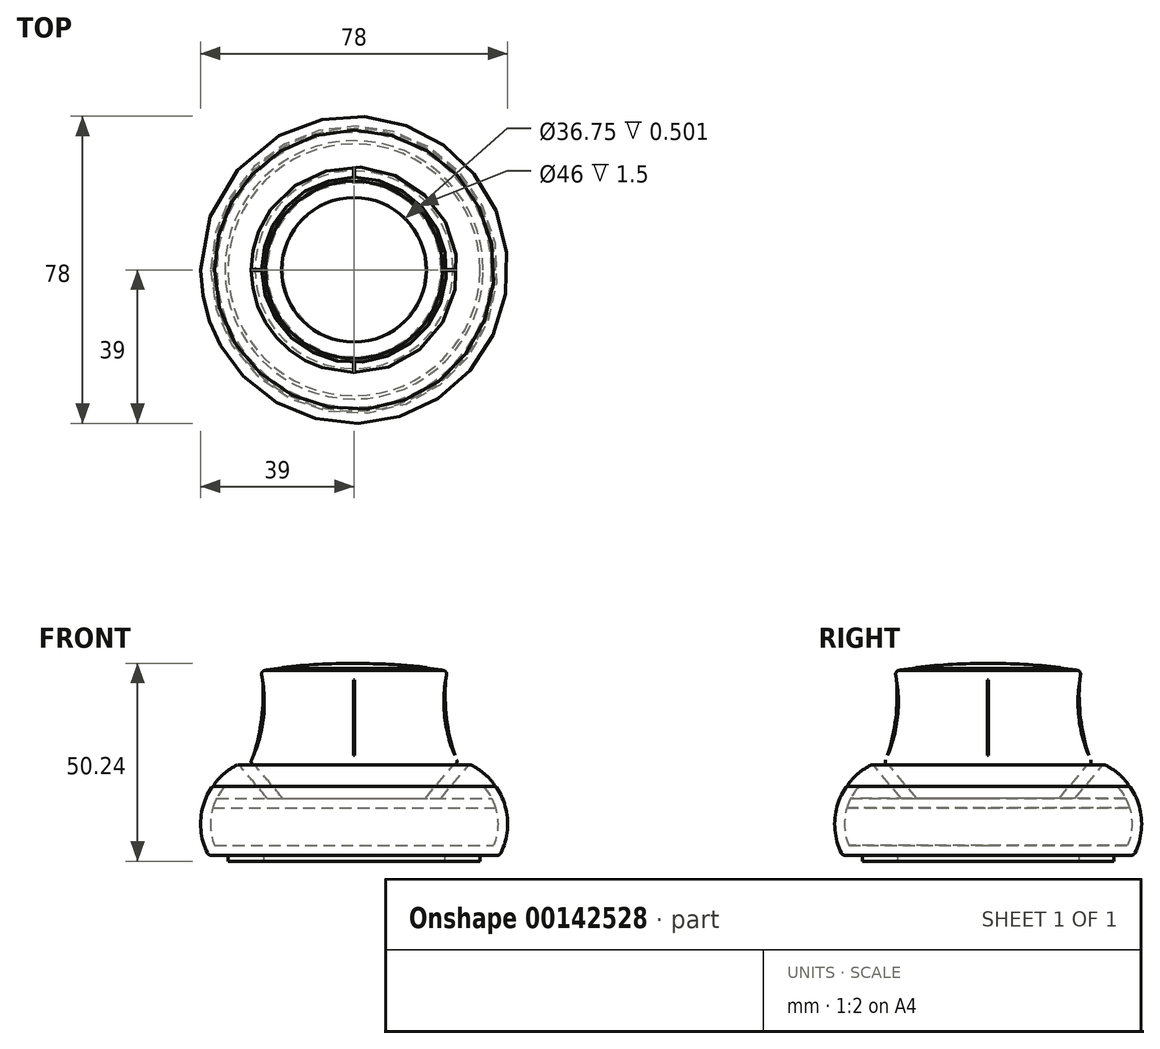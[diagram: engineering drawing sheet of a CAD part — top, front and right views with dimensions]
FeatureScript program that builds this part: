
annotation { "Feature Type Name" : "Feature", "Feature Type Description" : "" }
export const myFeature = defineFeature(function(context is Context, id is Id, definition is map)
    precondition{}
    {
        {
            var Q0;
            Q0=qCreatedBy(makeId("Front.planeOp"),FACE);
            var sketch = newSketch(context, id + "F0", { "sketchPlane" : qUnion([Q0])});
            skLineSegment(sketch, "E0", {"start": v(36.39, 0) * mm, "end": v(0, 0) * mm});
            skLineSegment(sketch, "E1", {"start": v(0, 0) * mm, "end": v(0, 17.5) * mm, "construction": true});
            skLineSegment(sketch, "E2", {"start": v(32.81, 17.5) * mm, "end": v(35.74, 17.5) * mm});
            skArc(sketch, "E3", {"start": v(35.4, 18.3) * mm, "mid": v(32.8, 20.95) * mm, "end": v(29.67, 22.95) * mm});
            skArc(sketch, "E4.0", {"start": v(35.42, 2.5) * mm, "mid": v(36.29, 10.38) * mm, "end": v(32.81, 17.5) * mm});
            skLineSegment(sketch, "E4.1", {"start": v(35.42, 2.5) * mm, "end": v(0, 2.5) * mm});
            skPoint(sketch, "E5.visualSharp", {"position": v(37, 0) * mm});
            skArc(sketch, "E5.filletArc", {"start": v(36.39, 0) * mm, "mid": v(36.92, 0.15) * mm, "end": v(37.29, 0.56) * mm});
            skPoint(sketch, "E6.newPointA", {"position": v(36, 17.5) * mm});
            skLineSegment(sketch, "E7", {"start": v(0, 0) * mm, "end": v(0, 2.5) * mm});
            skLineSegment(sketch, "E8", {"start": v(23, 0) * mm, "end": v(23, -1.5) * mm});
            skLineSegment(sketch, "E9", {"start": v(23, -1.5) * mm, "end": v(32, -1.5) * mm});
            skLineSegment(sketch, "E10", {"start": v(32, -1.5) * mm, "end": v(32, 0) * mm});
            skLineSegment(sketch, "E11", {"start": v(29.07, 22.82) * mm, "end": v(22.09, 14.5) * mm});
            skLineSegment(sketch, "E12", {"start": v(0, 14.5) * mm, "end": v(34.9, 14.5) * mm});
            skLineSegment(sketch, "E13", {"start": v(0, 14.5) * mm, "end": v(0, 12) * mm});
            skLineSegment(sketch, "E14", {"start": v(0, 12) * mm, "end": v(35.9, 12) * mm});
            skArc(sketch, "E15.filletArc", {"start": v(35, 17.5) * mm, "mid": v(35.46, 17.78) * mm, "end": v(35.4, 18.3) * mm});
            skArc(sketch, "E16", {"start": v(37.29, 0.56) * mm, "mid": v(38.96, 9.07) * mm, "end": v(36.15, 17.28) * mm});
            skArc(sketch, "E17.filletArc", {"start": v(36.15, 17.28) * mm, "mid": v(35.97, 17.44) * mm, "end": v(35.74, 17.5) * mm});
            skPoint(sketch, "E18.visualSharp", {"position": v(29.32, 23.12) * mm});
            skArc(sketch, "E18.filletArc", {"start": v(29.67, 22.95) * mm, "mid": v(29.35, 22.99) * mm, "end": v(29.07, 22.82) * mm});
            skLineSegment(sketch, "E19", {"start": v(0, 22.99) * mm, "end": v(25.13, 22.83) * mm});
            skPoint(sketch, "E19.startSnap0", {"position": v(29.35, 22.99) * mm});
            skLineSegment(sketch, "E20", {"start": v(0, 14.5) * mm, "end": v(0, 46.99) * mm});
            skLineSegment(sketch, "E21", {"start": v(0, 46.99) * mm, "end": v(18.38, 46.99) * mm});
            skArc(sketch, "E22", {"start": v(23.49, 45.8) * mm, "mid": v(23.06, 34.82) * mm, "end": v(26.05, 24.25) * mm});
            skPoint(sketch, "E23.visualSharp", {"position": v(23.75, 46.99) * mm});
            skArc(sketch, "E23.filletArc", {"start": v(23.49, 45.8) * mm, "mid": v(23.28, 46.62) * mm, "end": v(22.5, 46.99) * mm});
            skPoint(sketch, "E24.visualSharp", {"position": v(26.75, 22.82) * mm});
            skArc(sketch, "E24.filletArc", {"start": v(25.13, 22.83) * mm, "mid": v(25.98, 23.3) * mm, "end": v(26.05, 24.25) * mm});
            skLineSegment(sketch, "E25", {"start": v(25.13, 22.83) * mm, "end": v(18.14, 14.5) * mm});
            skArc(sketch, "E26", {"start": v(23.26, 44.49) * mm, "mid": v(23.48, 34.8) * mm, "end": v(25.57, 25.32) * mm});
            skArc(sketch, "E27", {"start": v(22.5, 46.99) * mm, "mid": v(20.44, 47.25) * mm, "end": v(18.38, 47.5) * mm});
            skLineSegment(sketch, "E28", {"start": v(18.38, 46.99) * mm, "end": v(18.38, 47.5) * mm});
            skArc(sketch, "E29.0", {"start": v(18.2, 47.76) * mm, "mid": v(9.12, 48.5) * mm, "end": v(0, 48.74) * mm});
            skPoint(sketch, "E30.orphan", {"position": v(0, 48.49) * mm});
            skLineSegment(sketch, "E31", {"start": v(18.38, 47.5) * mm, "end": v(18.38, 47.57) * mm});
            skLineSegment(sketch, "E32", {"start": v(0, 46.99) * mm, "end": v(0, 48.74) * mm});
            skPoint(sketch, "E33.visualSharp", {"position": v(18.38, 47.74) * mm});
            skArc(sketch, "E33.filletArc", {"start": v(18.38, 47.57) * mm, "mid": v(18.33, 47.7) * mm, "end": v(18.2, 47.76) * mm});
            skLineSegment(sketch, "E34", {"start": v(38.66, 42.16) * mm, "end": v(52.9, 49.44) * mm});
            skSolve(sketch);
        }
        {
            var Q0;
            Q0=makeQuery(id+"F0.imprint","IMPRINT",FACE,{"disambiguationData":[TD([[makeQuery(id+"F0.imprint","IMPRINT",EDGE,{"derivedFrom":sQuery(id+"F0.wireOp",EDGE,"E2")}),-1.0]])]});
            var Q1;
            Q1=sQuery(id+"F0.wireOp",EDGE,"E1");
            revolve(context, id + "F1", {"entities" : qUnion([Q0]), "axis" : qUnion([Q1]), "revolveType" : RevolveType.FULL});
        }
        {
            var Q0;
            {var subQ0=sQuery(id+"F0.wireOp",EDGE,"E8");Q0=makeQuery(id+"F0.imprint","IMPRINT",FACE,{"disambiguationData":[TD([[makeQuery(id+"F0.imprint","IMPRINT",EDGE,{"derivedFrom":subQ0}),1.0]])]});}
            var Q1;
            Q1=sQuery(id+"F0.wireOp",EDGE,"E1");
            revolve(context, id + "F2", {"entities" : qUnion([Q0]), "axis" : qUnion([Q1]), "revolveType" : RevolveType.FULL});
        }
        {
            var Q0;
            Q0=makeQuery(id+"F0.imprint","IMPRINT",FACE,{"disambiguationData":[TD([[makeQuery(id+"F0.imprint","IMPRINT",EDGE,{"derivedFrom":sQuery(id+"F0.wireOp",EDGE,"E3")}),1.0]])]});
            var Q1;
            Q1=makeQuery(id+"F0.imprint","IMPRINT",FACE,{"disambiguationData":[TD([[makeQuery(id+"F0.imprint","IMPRINT",EDGE,{"derivedFrom":sQuery(id+"F0.wireOp",EDGE,"E21")}),1.0]])]});
            var Q2;
            Q2=sQuery(id+"F0.wireOp",EDGE,"E1");
            revolve(context, id + "F3", {"entities" : qUnion([Q0, Q1]), "axis" : qUnion([Q2]), "revolveType" : RevolveType.FULL});
        }
        {
            var Q0;
            {var subQ0=sQuery(id+"F0.wireOp",EDGE,"E13");Q0=makeQuery(id+"F0.imprint","IMPRINT",FACE,{"disambiguationData":[TD([[makeQuery(id+"F0.imprint","IMPRINT",EDGE,{"derivedFrom":subQ0}),1.0]])]});}
            var Q1;
            Q1=sQuery(id+"F0.wireOp",EDGE,"E1");
            revolve(context, id + "F4", {"entities" : qUnion([Q0]), "axis" : qUnion([Q1]), "revolveType" : RevolveType.FULL});
        }
        {
            var Q0;
            {var subQ2=sQuery(id+"F0.wireOp",EDGE,"E19");Q0=makeQuery(id+"F0.imprint","IMPRINT",FACE,{"disambiguationData":[TD([[makeQuery(id+"F0.imprint","IMPRINT",EDGE,{"derivedFrom":subQ2}),1.0]])]});}
            var Q1;
            {var subQ4=sQuery(id+"F0.wireOp",EDGE,"E19");Q1=makeQuery(id+"F0.imprint","IMPRINT",FACE,{"disambiguationData":[TD([[makeQuery(id+"F0.imprint","IMPRINT",EDGE,{"derivedFrom":subQ4}),-1.0]])]});}
            var Q2;
            Q2=sQuery(id+"F0.wireOp",EDGE,"E20");
            revolve(context, id + "F5", {"entities" : qUnion([Q0, Q1]), "axis" : qUnion([Q2]), "revolveType" : RevolveType.FULL});
        }
        {
            var Q0;
            {var subQ0=sQuery(id+"F0.wireOp",EDGE,"E26");Q0=makeQuery(id+"F0.imprint","IMPRINT",FACE,{"disambiguationData":[TD([[makeQuery(id+"F0.imprint","IMPRINT",EDGE,{"derivedFrom":subQ0}),-1.0]])]});}
            extrude(context, id + "F6", {"entities" : qUnion([Q0]), "endBound" : BoundingType.SYMMETRIC, "depth" : .25 * mm});
        }
        {
            var Q0;
            Q0=makeQuery(id+"F6.opExtrude","SWEPT_BODY",BODY,{"disambiguationData":[OSD([sQuery(id+"F0.wireOp",EDGE,"E22"),sQuery(id+"F0.wireOp",EDGE,"E26")])]});
            var Q1;
            Q1=sQuery(id+"F0.wireOp",EDGE,"E20");
            circularPattern(context, id + "F7", {"operationType" : NewBodyOperationType.ADD, "entities" : qUnion([Q0]), "axis" : qUnion([Q1]), "angle" : 90 * degree, "instanceCount" : 4});
        }
    });
